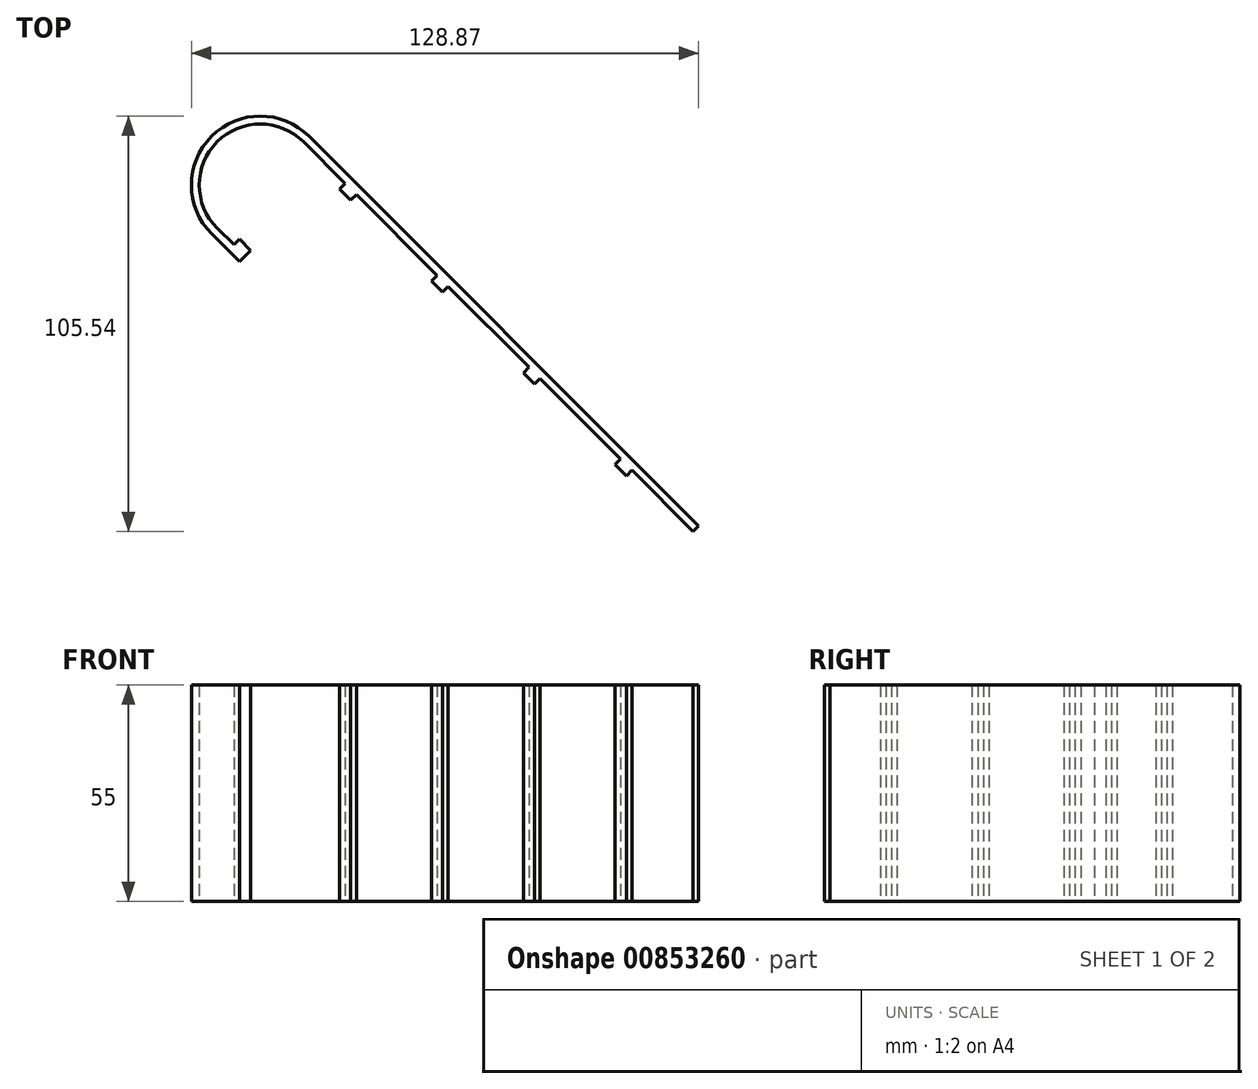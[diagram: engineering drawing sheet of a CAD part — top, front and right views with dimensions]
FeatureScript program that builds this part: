
annotation { "Feature Type Name" : "Feature", "Feature Type Description" : "" }
export const myFeature = defineFeature(function(context is Context, id is Id, definition is map)
    precondition{}
    {
        {
            var Q0;
            Q0=qCreatedBy(makeId("Top.planeOp"),FACE);
            var sketch = newSketch(context, id + "F0", { "sketchPlane" : qUnion([Q0])});
            skLineSegment(sketch, "E0", {"start": v(-75, 75) * mm, "end": v(-75, -75) * mm, "construction": true});
            skLineSegment(sketch, "E1", {"start": v(-75, -75) * mm, "end": v(75, -75) * mm, "construction": true});
            skLineSegment(sketch, "E2", {"start": v(75, -75) * mm, "end": v(75, 75) * mm, "construction": true});
            skLineSegment(sketch, "E3", {"start": v(75, 75) * mm, "end": v(-75, 75) * mm, "construction": true});
            skLineSegment(sketch, "E4", {"start": v(-75, 75) * mm, "end": v(75, -75) * mm, "construction": true});
            skLineSegment(sketch, "E5", {"start": v(64.65, -39.9) * mm, "end": v(-34.34, 59.1) * mm});
            skArc(sketch, "E6", {"start": v(-34.34, 59.1) * mm, "mid": v(-59.1, 59.1) * mm, "end": v(-59.1, 34.34) * mm});
            skLineSegment(sketch, "E7", {"start": v(-59.1, 34.34) * mm, "end": v(-34.34, 59.1) * mm, "construction": true});
            skLineSegment(sketch, "E8", {"start": v(-59.1, 34.34) * mm, "end": v(-52.02, 27.27) * mm});
            skLineSegment(sketch, "E9", {"start": v(-52.02, 27.27) * mm, "end": v(-50.6, 28.68) * mm});
            skLineSegment(sketch, "E10", {"start": v(-53.43, 31.51) * mm, "end": v(-57.68, 35.76) * mm});
            skLineSegment(sketch, "E11", {"start": v(64.65, -39.9) * mm, "end": v(63.24, -41.32) * mm});
            skLineSegment(sketch, "E12", {"start": v(63.24, -41.32) * mm, "end": v(47.68, -25.76) * mm});
            skArc(sketch, "E13", {"start": v(-57.68, 35.76) * mm, "mid": v(-57.68, 57.68) * mm, "end": v(-35.76, 57.68) * mm});
            skLineSegment(sketch, "E14", {"start": v(-25.15, 47.07) * mm, "end": v(-26.56, 45.66) * mm});
            skLineSegment(sketch, "E15", {"start": v(-26.56, 45.66) * mm, "end": v(-23.73, 42.83) * mm});
            skLineSegment(sketch, "E16", {"start": v(-23.73, 42.83) * mm, "end": v(-22.32, 44.24) * mm});
            skLineSegment(sketch, "E17.1.0.0", {"start": v(-1.81, 23.73) * mm, "end": v(-3.23, 22.32) * mm});
            skLineSegment(sketch, "E17.1.0.1", {"start": v(-3.23, 22.32) * mm, "end": v(-0.4, 19.5) * mm});
            skLineSegment(sketch, "E17.1.0.2", {"start": v(-0.4, 19.5) * mm, "end": v(1.01, 20.9) * mm});
            skLineSegment(sketch, "E17.2.0.0", {"start": v(21.52, 0.4) * mm, "end": v(20.1, -1.01) * mm});
            skLineSegment(sketch, "E17.2.0.1", {"start": v(20.1, -1.01) * mm, "end": v(22.93, -3.84) * mm});
            skLineSegment(sketch, "E17.2.0.2", {"start": v(22.93, -3.84) * mm, "end": v(24.35, -2.43) * mm});
            skLineSegment(sketch, "E17.3.0.0", {"start": v(44.85, -22.93) * mm, "end": v(43.44, -24.35) * mm});
            skLineSegment(sketch, "E17.3.0.1", {"start": v(43.44, -24.35) * mm, "end": v(46.27, -27.18) * mm});
            skLineSegment(sketch, "E17.3.0.2", {"start": v(46.27, -27.18) * mm, "end": v(47.68, -25.76) * mm});
            skLineSegment(sketch, "E17.direction1", {"start": v(-26.56, 45.66) * mm, "end": v(-3.23, 22.32) * mm, "construction": true});
            skLineSegment(sketch, "E18", {"start": v(-50.6, 28.68) * mm, "end": v(-49.2, 30.1) * mm});
            skLineSegment(sketch, "E19", {"start": v(-49.2, 30.1) * mm, "end": v(-52.02, 32.93) * mm});
            skLineSegment(sketch, "E20", {"start": v(-52.02, 32.93) * mm, "end": v(-53.43, 31.51) * mm});
            skLineSegment(sketch, "E21.trimOffspring", {"start": v(-25.15, 47.07) * mm, "end": v(-35.76, 57.68) * mm});
            skLineSegment(sketch, "E22.trimOffspring", {"start": v(-1.81, 23.73) * mm, "end": v(-22.32, 44.24) * mm});
            skLineSegment(sketch, "E23.trimOffspring", {"start": v(21.52, 0.4) * mm, "end": v(1.01, 20.9) * mm});
            skLineSegment(sketch, "E24.trimOffspring", {"start": v(44.85, -22.93) * mm, "end": v(24.35, -2.43) * mm});
            skSolve(sketch);
        }
        {
            var Q0;
            Q0=qSketchRegion(id+"F0",true);
            extrude(context, id + "F1", {"entities" : qUnion([Q0]), "depth" : 55 * mm});
        }
    });
